annotation { "Feature Type Name" : "Feature", "Feature Type Description" : "" }
export const myFeature = defineFeature(function(context is Context, id is Id, definition is map)
    precondition{}
    {
        {
            var Q0;
            Q0=qCreatedBy(makeId("Front.planeOp"),FACE);
            var sketch = newSketch(context, id + "F0", { "sketchPlane" : qUnion([Q0])});
            skArc(sketch, "E0", {"start": v(0, -50.8) * mm, "mid": v(35.92, -35.92) * mm, "end": v(50.8, 0) * mm});
            skLineSegment(sketch, "E1", {"start": v(0, 50.8) * mm, "end": v(50.8, 50.8) * mm});
            skLineSegment(sketch, "E2", {"start": v(50.8, 50.8) * mm, "end": v(50.8, 0) * mm});
            skLineSegment(sketch, "E3", {"start": v(-50.8, 0) * mm, "end": v(-50.8, -50.8) * mm});
            skLineSegment(sketch, "E4", {"start": v(-50.8, -50.8) * mm, "end": v(0, -50.8) * mm});
            skArc(sketch, "E5.trimOffspring", {"start": v(0, 50.8) * mm, "mid": v(-35.92, 35.92) * mm, "end": v(-50.8, 0) * mm});
            skSolve(sketch);
        }
        {
            var Q0;
            Q0 = qSketchRegion(id + "F0", true);
            extrude(context, id + "F1", {"entities" : qUnion([Q0]), "depth" : 50.8 * mm});
        }
        {
            var Q0;
            Q0=makeQuery(id+"F1.opExtrude","CAP_FACE",FACE,{"disambiguationData":[OSD([sQuery(id+"F0.wireOp",EDGE,"E0"),sQuery(id+"F0.wireOp",EDGE,"E1"),sQuery(id+"F0.wireOp",EDGE,"E2"),sQuery(id+"F0.wireOp",EDGE,"E3"),sQuery(id+"F0.wireOp",EDGE,"E4"),sQuery(id+"F0.wireOp",EDGE,"E5.trimOffspring")])],"isStart":false});
            var sketch = newSketch(context, id + "F2", { "sketchPlane" : qUnion([Q0])});
            skCircle(sketch, "E6", {"center": v(0, 0) * mm, "radius": 45.37 * mm});
            skCircle(sketch, "E7.cCircle", {"center": v(0, 0) * mm, "radius": 32.63 * mm, "construction": true});
            skLineSegment(sketch, "E7.0", {"start": v(-27.13, 21.67) * mm, "end": v(-6.85, 34.04) * mm});
            skLineSegment(sketch, "E7.1", {"start": v(-6.85, 34.04) * mm, "end": v(16.63, 30.48) * mm});
            skLineSegment(sketch, "E7.2", {"start": v(16.63, 30.48) * mm, "end": v(32.33, 12.66) * mm});
            skLineSegment(sketch, "E7.3", {"start": v(32.33, 12.66) * mm, "end": v(32.9, -11.09) * mm});
            skLineSegment(sketch, "E7.4", {"start": v(32.9, -11.09) * mm, "end": v(18.08, -29.64) * mm});
            skLineSegment(sketch, "E7.5", {"start": v(18.08, -29.64) * mm, "end": v(-5.2, -34.33) * mm});
            skLineSegment(sketch, "E7.6", {"start": v(-5.2, -34.33) * mm, "end": v(-26.05, -22.95) * mm});
            skLineSegment(sketch, "E7.7", {"start": v(-26.05, -22.95) * mm, "end": v(-34.71, -0.84) * mm});
            skLineSegment(sketch, "E7.8", {"start": v(-34.71, -0.84) * mm, "end": v(-27.13, 21.67) * mm});
            skPoint(sketch, "E7.0.midPoint", {"position": v(-16.99, 27.86) * mm});
            skSolve(sketch);
        }
        {
            var Q0;
            Q0 = qSketchRegion(id + "F2", true);
            extrude(context, id + "F3", {"entities" : qUnion([Q0]), "operationType" : NewBodyOperationType.ADD, "depth" : 25.4 * mm});
        }
        {
            var Q0;
            Q0=qCreatedBy(makeId("Front.planeOp"),FACE);
            var sketch = newSketch(context, id + "F4", { "sketchPlane" : qUnion([Q0])});
            skText(sketch, "E8", { "text": "JATT MEHKMA\n", "fontName": "OpenSans-BoldItalic.ttf"});
            const initialGuessF4  = {"E8": [-0.18373, -0.02627, 1, 0, 0.02608]};
            skSetInitialGuess(sketch, initialGuessF4);
            skSolve(sketch);
        }
        {
            var Q0;
            Q0 = qSketchRegion(id + "F4", true);
            extrude(context, id + "F5", {"entities" : qUnion([Q0]), "operationType" : NewBodyOperationType.ADD, "depth" : 127 * mm});
        }
    });